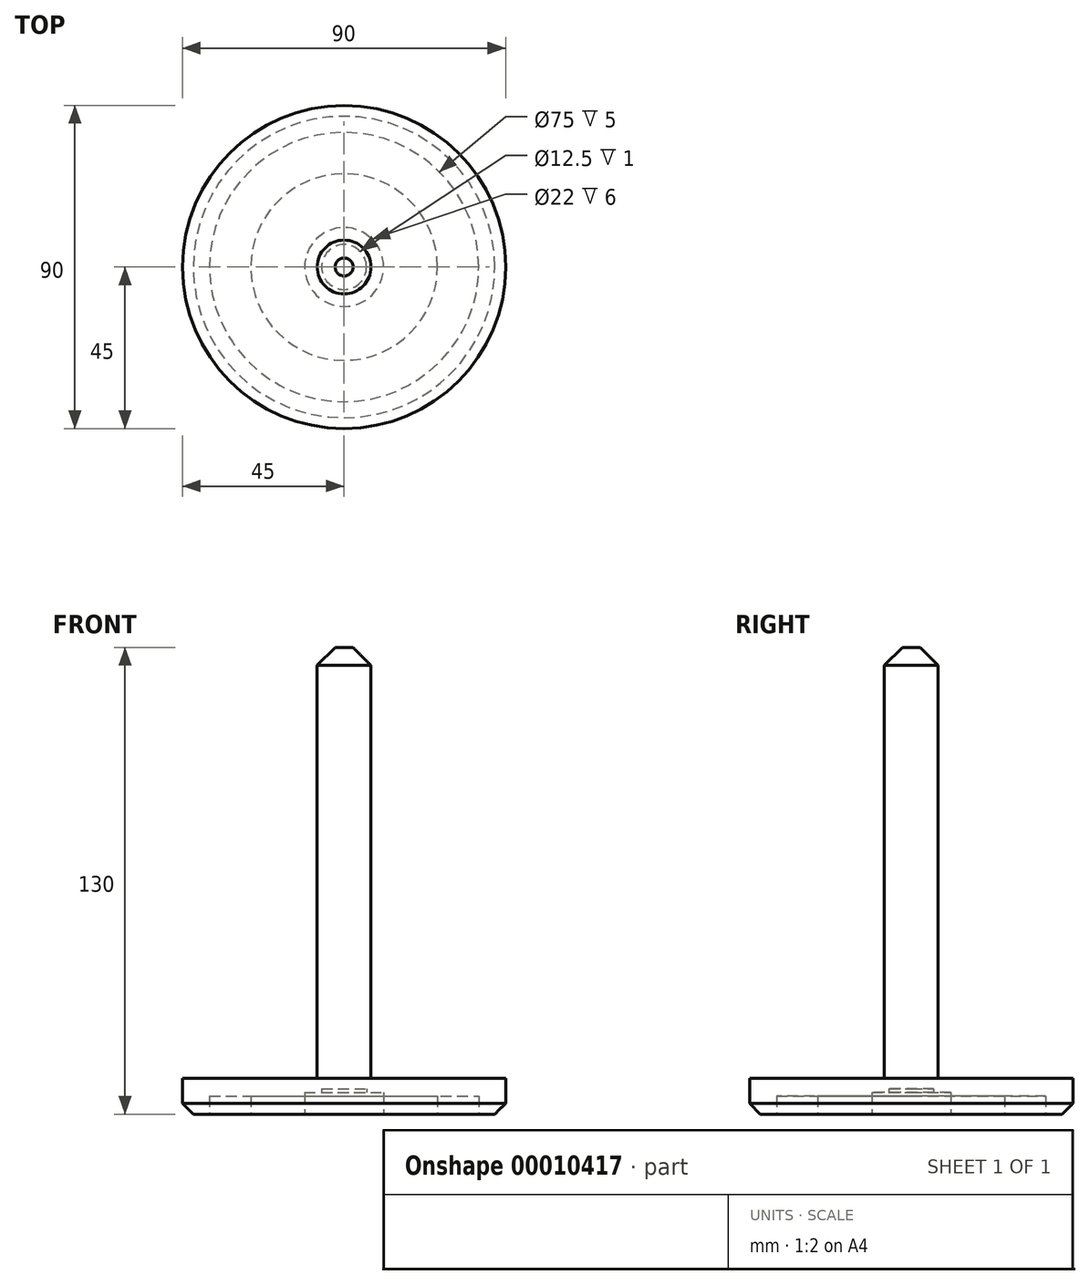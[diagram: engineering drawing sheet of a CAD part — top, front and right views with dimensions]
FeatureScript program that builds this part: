
annotation { "Feature Type Name" : "Feature", "Feature Type Description" : "" }
export const myFeature = defineFeature(function(context is Context, id is Id, definition is map)
    precondition{}
    {
        {
            var Q0;
            Q0=qCreatedBy(makeId("Top.planeOp"),FACE);
            var sketch = newSketch(context, id + "F0", { "sketchPlane" : qUnion([Q0])});
            skCircle(sketch, "E0", {"center": v(0, 0) * mm, "radius": 45 * mm});
            skSolve(sketch);
        }
        {
            var Q0;
            Q0=makeQuery(id+"F0.imprint","IMPRINT",FACE,{"disambiguationData":[TD([[makeQuery(id+"F0.imprint","IMPRINT",EDGE,{"derivedFrom":sQuery(id+"F0.wireOp",EDGE,"E0")}),1.0]])]});
            extrude(context, id + "F1", {"entities" : qUnion([Q0]), "depth" : 10 * mm});
        }
        {
            var Q0;
            Q0=makeQuery(id+"F1.opExtrude","CAP_FACE",FACE,{"disambiguationData":[OSD([sQuery(id+"F0.wireOp",EDGE,"E0")])],"isStart":false});
            var sketch = newSketch(context, id + "F2", { "sketchPlane" : qUnion([Q0])});
            skCircle(sketch, "E1", {"center": v(0, 0) * mm, "radius": 7.5 * mm});
            skSolve(sketch);
        }
        {
            var Q0;
            Q0=makeQuery(id+"F2.imprint","IMPRINT",FACE,{"disambiguationData":[TD([[makeQuery(id+"F2.imprint","IMPRINT",EDGE,{"derivedFrom":sQuery(id+"F2.wireOp",EDGE,"E1")}),1.0]])]});
            extrude(context, id + "F3", {"entities" : qUnion([Q0]), "operationType" : NewBodyOperationType.ADD, "depth" : 120 * mm});
        }
        {
            var Q0;
            Q0=makeQuery(id+"F3.opExtrude","CAP_EDGE",EDGE,{"disambiguationData":[OSD([sQuery(id+"F2.wireOp",EDGE,"E1")])],"isStart":false});
            chamfer(context, id + "F4", {"entities" : qUnion([Q0]), "width" : 5 * mm, "tangentPropagation" : true});
        }
        {
            var Q0;
            Q0=makeQuery(id+"F1.opExtrude","CAP_FACE",FACE,{"disambiguationData":[OSD([sQuery(id+"F0.wireOp",EDGE,"E0")])],"isStart":true});
            var sketch = newSketch(context, id + "F5", { "sketchPlane" : qUnion([Q0])});
            skCircle(sketch, "E2", {"center": v(0, 0) * mm, "radius": 11 * mm});
            skSolve(sketch);
        }
        {
            var Q0;
            Q0=makeQuery(id+"F5.imprint","IMPRINT",FACE,{"disambiguationData":[TD([[makeQuery(id+"F5.imprint","IMPRINT",EDGE,{"derivedFrom":sQuery(id+"F5.wireOp",EDGE,"E2")}),1.0]])]});
            extrude(context, id + "F6", {"entities" : qUnion([Q0]), "operationType" : NewBodyOperationType.REMOVE, "oppositeDirection" : true, "depth" : 6 * mm});
        }
        {
            var Q0;
            Q0=makeQuery(id+"F6.boolean.opBoolean","COPY",FACE,{"derivedFrom":makeQuery(id+"F6.opExtrude","CAP_FACE",FACE,{"disambiguationData":[OSD([sQuery(id+"F5.wireOp",EDGE,"E2")])],"isStart":false})});
            var sketch = newSketch(context, id + "F7", { "sketchPlane" : qUnion([Q0])});
            skCircle(sketch, "E3", {"center": v(0, 0) * mm, "radius": 6.25 * mm});
            skSolve(sketch);
        }
        {
            var Q0;
            Q0=makeQuery(id+"F7.imprint","IMPRINT",FACE,{"disambiguationData":[TD([[makeQuery(id+"F7.imprint","IMPRINT",EDGE,{"derivedFrom":sQuery(id+"F7.wireOp",EDGE,"E3")}),1.0]])]});
            extrude(context, id + "F8", {"entities" : qUnion([Q0]), "operationType" : NewBodyOperationType.REMOVE, "oppositeDirection" : true, "depth" : 1 * mm});
        }
        {
            var Q0;
            Q0=makeQuery(id+"F1.opExtrude","CAP_FACE",FACE,{"disambiguationData":[OSD([sQuery(id+"F0.wireOp",EDGE,"E0")])],"isStart":true});
            var sketch = newSketch(context, id + "F9", { "sketchPlane" : qUnion([Q0])});
            skCircle(sketch, "E4", {"center": v(0, 0) * mm, "radius": 26 * mm});
            skCircle(sketch, "E5", {"center": v(0, 0) * mm, "radius": 37.5 * mm});
            skSolve(sketch);
        }
        {
            var Q0;
            Q0=makeQuery(id+"F9.imprint","IMPRINT",FACE,{"disambiguationData":[TD([[makeQuery(id+"F9.imprint","IMPRINT",EDGE,{"derivedFrom":sQuery(id+"F9.wireOp",EDGE,"E4")}),-1.0]])]});
            extrude(context, id + "F10", {"entities" : qUnion([Q0]), "operationType" : NewBodyOperationType.REMOVE, "oppositeDirection" : true, "depth" : 5 * mm});
        }
        {
            var Q0;
            Q0=makeQuery(id+"F1.opExtrude","CAP_EDGE",EDGE,{"disambiguationData":[OSD([sQuery(id+"F0.wireOp",EDGE,"E0")])],"isStart":true});
            chamfer(context, id + "F11", {"entities" : qUnion([Q0]), "width" : 3 * mm, "tangentPropagation" : true});
        }
    });
